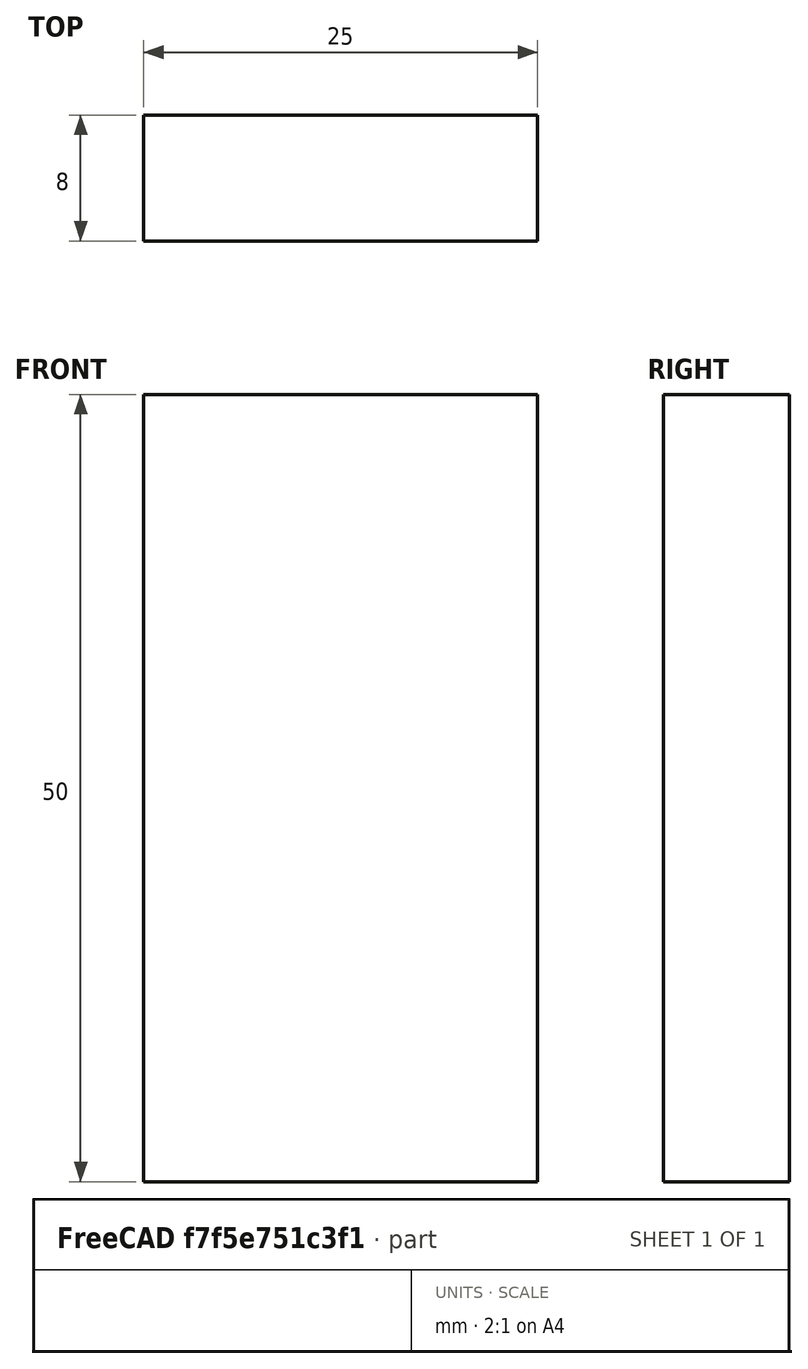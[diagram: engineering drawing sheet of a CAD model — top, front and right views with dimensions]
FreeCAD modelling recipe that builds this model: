
FCSTD DOCUMENT  (FreeCAD 0.15R4671 (Git))
Label: Flat Bar 25x8 EN10058 S235JR
License: All rights reserved
LicenseURL: http://en.wikipedia.org/wiki/All_rights_reserved
objects: Sketcher::SketchObject×1, Part::Extrusion×1
note: 2 computed .brp shape members not serialized (recipe doc carries the construction recipe); baked Part::Feature solids carry a one-line shape summary decoded from their .brp

FEATURE [Sketcher::SketchObject] Sketch
  sketch-geometry (4):
    g0: LineSegment StartX=-12.5 StartY=-4 StartZ=0 EndX=12.5 EndY=-4 EndZ=0
    g1: LineSegment StartX=12.5 StartY=-4 StartZ=0 EndX=12.5 EndY=4 EndZ=0
    g2: LineSegment StartX=12.5 StartY=4 StartZ=0 EndX=-12.5 EndY=4 EndZ=0
    g3: LineSegment StartX=-12.5 StartY=4 StartZ=0 EndX=-12.5 EndY=-4 EndZ=0
  constraints (12):
    c: Coincident(g0,g1)
    c: Coincident(g1,g2)
    c: Coincident(g2,g3)
    c: Coincident(g3,g0)
    c: Horizontal(g0)
    c: Horizontal(g2)
    c: Vertical(g1)
    c: Vertical(g3)
    c: Symmetric(g1,g2,g-2)
    c: Symmetric(g0,g1,g-1)
    c: DistanceY(g1) = 8
    c: DistanceX(g0) = 25
FEATURE [Part::Extrusion] Extrude  label="Flat Bar 25x8 EN10058 S235JR"
  Base = -> Sketch
  Dir = (0,0,50)
  Solid = true
